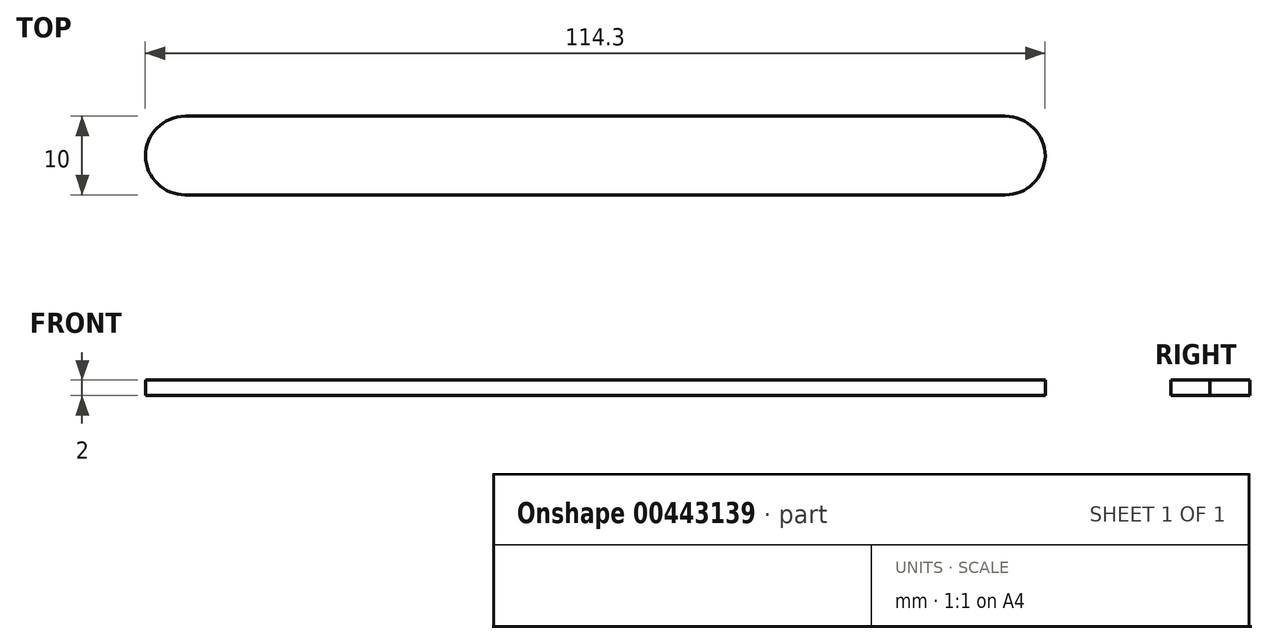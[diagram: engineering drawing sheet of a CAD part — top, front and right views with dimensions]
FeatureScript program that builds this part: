
annotation { "Feature Type Name" : "Feature", "Feature Type Description" : "" }
export const myFeature = defineFeature(function(context is Context, id is Id, definition is map)
    precondition{}
    {
        {
            var Q0;
            Q0=qCreatedBy(makeId("Top.planeOp"),FACE);
            var sketch = newSketch(context, id + "F0", { "sketchPlane" : qUnion([Q0])});
            skLineSegment(sketch, "E0.bottom", {"start": v(-59.5, -42.44) * mm, "end": v(54.8, -42.44) * mm});
            skLineSegment(sketch, "E0.top", {"start": v(-59.5, -32.44) * mm, "end": v(54.8, -32.44) * mm});
            skLineSegment(sketch, "E0.left", {"start": v(-59.5, -42.44) * mm, "end": v(-59.5, -32.44) * mm});
            skLineSegment(sketch, "E0.right", {"start": v(54.8, -42.44) * mm, "end": v(54.8, -32.44) * mm});
            skSolve(sketch);
        }
        {
            var Q0;
            Q0=makeQuery(id+"F0.imprint","IMPRINT",FACE,{"disambiguationData":[TD([[makeQuery(id+"F0.imprint","IMPRINT",EDGE,{"derivedFrom":sQuery(id+"F0.wireOp",EDGE,"E0.bottom")}),1.0]])]});
            extrude(context, id + "F1", {"entities" : qUnion([Q0]), "depth" : 2 * mm});
        }
        {
            var Q0;
            Q0=makeQuery(id+"F1.opExtrude","SWEPT_EDGE",EDGE,{"disambiguationData":[OSD([sQuery(id+"F0.wireOp",EDGE,"E0.top"),sQuery(id+"F0.wireOp",EDGE,"E0.left")])]});
            fillet(context, id + "F2", {"entities" : qUnion([Q0]), "radius" : 5.08 * mm, "tangentPropagation" : true, "allowEdgeOverflow" : false});
        }
        {
            var Q0;
            Q0=makeQuery(id+"F1.opExtrude","SWEPT_EDGE",EDGE,{"disambiguationData":[OSD([sQuery(id+"F0.wireOp",EDGE,"E0.top"),sQuery(id+"F0.wireOp",EDGE,"E0.right")])]});
            fillet(context, id + "F3", {"entities" : qUnion([Q0]), "radius" : 5.08 * mm, "tangentPropagation" : true, "allowEdgeOverflow" : false});
        }
        {
            var Q0;
            Q0=makeQuery(id+"F1.opExtrude","SWEPT_EDGE",EDGE,{"disambiguationData":[OSD([sQuery(id+"F0.wireOp",EDGE,"E0.bottom"),sQuery(id+"F0.wireOp",EDGE,"E0.left")])]});
            fillet(context, id + "F4", {"entities" : qUnion([Q0]), "radius" : 5.08 * mm, "tangentPropagation" : true, "allowEdgeOverflow" : false});
        }
        {
            var Q0;
            Q0=makeQuery(id+"F1.opExtrude","SWEPT_EDGE",EDGE,{"disambiguationData":[OSD([sQuery(id+"F0.wireOp",EDGE,"E0.bottom"),sQuery(id+"F0.wireOp",EDGE,"E0.right")])]});
            fillet(context, id + "F5", {"entities" : qUnion([Q0]), "radius" : 5.08 * mm, "tangentPropagation" : true, "allowEdgeOverflow" : false});
        }
    });
